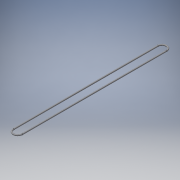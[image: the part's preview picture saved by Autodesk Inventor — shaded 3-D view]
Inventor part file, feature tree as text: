
AUTODESK INVENTOR PART (.ipt)
format: ipt  version: 2019 (Build 230136000, 136)  size: 118,784 bytes
history: native  units: mm
features: sketch x3, revolve x2, projected_geometry x2, extrude x1
ambient origin geometry x8: Origin, YZ Plane, XZ Plane, XY Plane, X Axis, Y Axis, Z Axis, Center Point
bodies: Body1 (feature_tree)
feature tree (8):
  revolve  "Revolution1"  [1 undecoded]
  extrude  "Extrusion1"  Depth=100.0mm TaperAngle=0.0deg
  revolve  "Revolution2"  [1 undecoded]
  sketch  "Sketch5"  dims[d8=1.0mm d9=3.0mm]
  sketch  "Sketch6"  dims[d10=180.0deg d11=100.0mm d12=0.0mm]
  projected_geometry  "Projected Loop1"
  projected_geometry  "Projected Loop2"
  sketch  "Sketch7"  dims[d13=180.0deg]
note: 2 required parameter values undecoded (feature->parameter linkage not recoverable at this tier; creation-order binding heuristic only, values carry confidence <= 0.55)